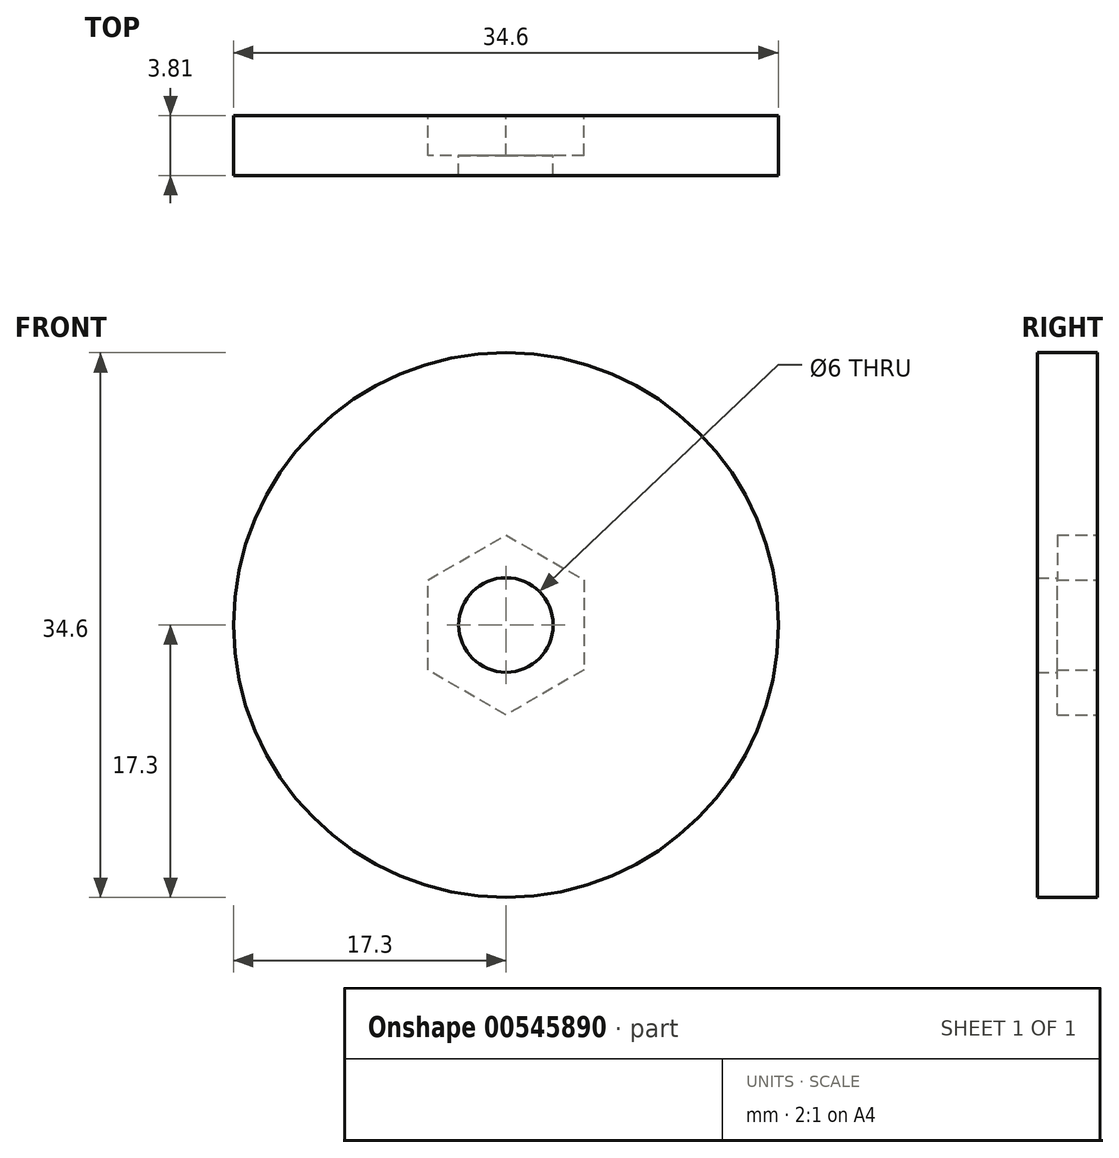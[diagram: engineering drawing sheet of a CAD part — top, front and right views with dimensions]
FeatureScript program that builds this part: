
annotation { "Feature Type Name" : "Feature", "Feature Type Description" : "" }
export const myFeature = defineFeature(function(context is Context, id is Id, definition is map)
    precondition{}
    {
        {
            var Q0;
            Q0=qCreatedBy(makeId("Front.planeOp"),FACE);
            var sketch = newSketch(context, id + "F0", { "sketchPlane" : qUnion([Q0])});
            skCircle(sketch, "E0", {"center": v(0, 0) * mm, "radius": 17.3 * mm});
            skSolve(sketch);
        }
        {
            var Q0;
            Q0 = qSketchRegion(id + "F0", true);
            extrude(context, id + "F1", {"entities" : qUnion([Q0]), "depth" : 3.8 * mm, "offsetDistance" : 25.4 * mm});
        }
        {
            var Q0;
            Q0=qCreatedBy(makeId("Front.planeOp"),FACE);
            var sketch = newSketch(context, id + "F2", { "sketchPlane" : qUnion([Q0])});
            skCircle(sketch, "E1.cCircle", {"center": v(0, 0) * mm, "radius": 4.95 * mm, "construction": true});
            skLineSegment(sketch, "E1.0", {"start": v(-4.95, -2.86) * mm, "end": v(-4.95, 2.86) * mm});
            skLineSegment(sketch, "E1.1", {"start": v(-4.95, 2.86) * mm, "end": v(0, 5.72) * mm});
            skLineSegment(sketch, "E1.2", {"start": v(0, 5.72) * mm, "end": v(4.95, 2.86) * mm});
            skLineSegment(sketch, "E1.3", {"start": v(4.95, 2.86) * mm, "end": v(4.95, -2.86) * mm});
            skLineSegment(sketch, "E1.4", {"start": v(4.95, -2.86) * mm, "end": v(0, -5.72) * mm});
            skLineSegment(sketch, "E1.5", {"start": v(0, -5.72) * mm, "end": v(-4.95, -2.86) * mm});
            skPoint(sketch, "E1.0.midPoint", {"position": v(-4.95, 0) * mm});
            skSolve(sketch);
        }
        {
            var Q0;
            Q0 = qSketchRegion(id + "F2", true);
            extrude(context, id + "F3", {"entities" : qUnion([Q0]), "operationType" : NewBodyOperationType.REMOVE, "depth" : 1.27 * mm, "offsetDistance" : 25.4 * mm});
        }
        {
            var Q0;
            Q0 = qSketchRegion(id + "F2", true);
            extrude(context, id + "F4", {"entities" : qUnion([Q0]), "operationType" : NewBodyOperationType.REMOVE, "depth" : 2.54 * mm, "offsetDistance" : 25.4 * mm});
        }
        {
            var Q0;
            Q0=makeQuery(id+"F1.opExtrude","CAP_FACE",FACE,{"disambiguationData":[OSD([sQuery(id+"F0.wireOp",EDGE,"E0")])],"isStart":true});
            var sketch = newSketch(context, id + "F5", { "sketchPlane" : qUnion([Q0])});
            skCircle(sketch, "E2", {"center": v(0, 0) * mm, "radius": 3 * mm});
            skSolve(sketch);
        }
        {
            var Q0;
            Q0 = qSketchRegion(id + "F5", true);
            extrude(context, id + "F6", {"entities" : qUnion([Q0]), "operationType" : NewBodyOperationType.REMOVE, "endBound" : BoundingType.THROUGH_ALL, "oppositeDirection" : true, "depth" : 25.4 * mm, "offsetDistance" : 25.4 * mm});
        }
    });
